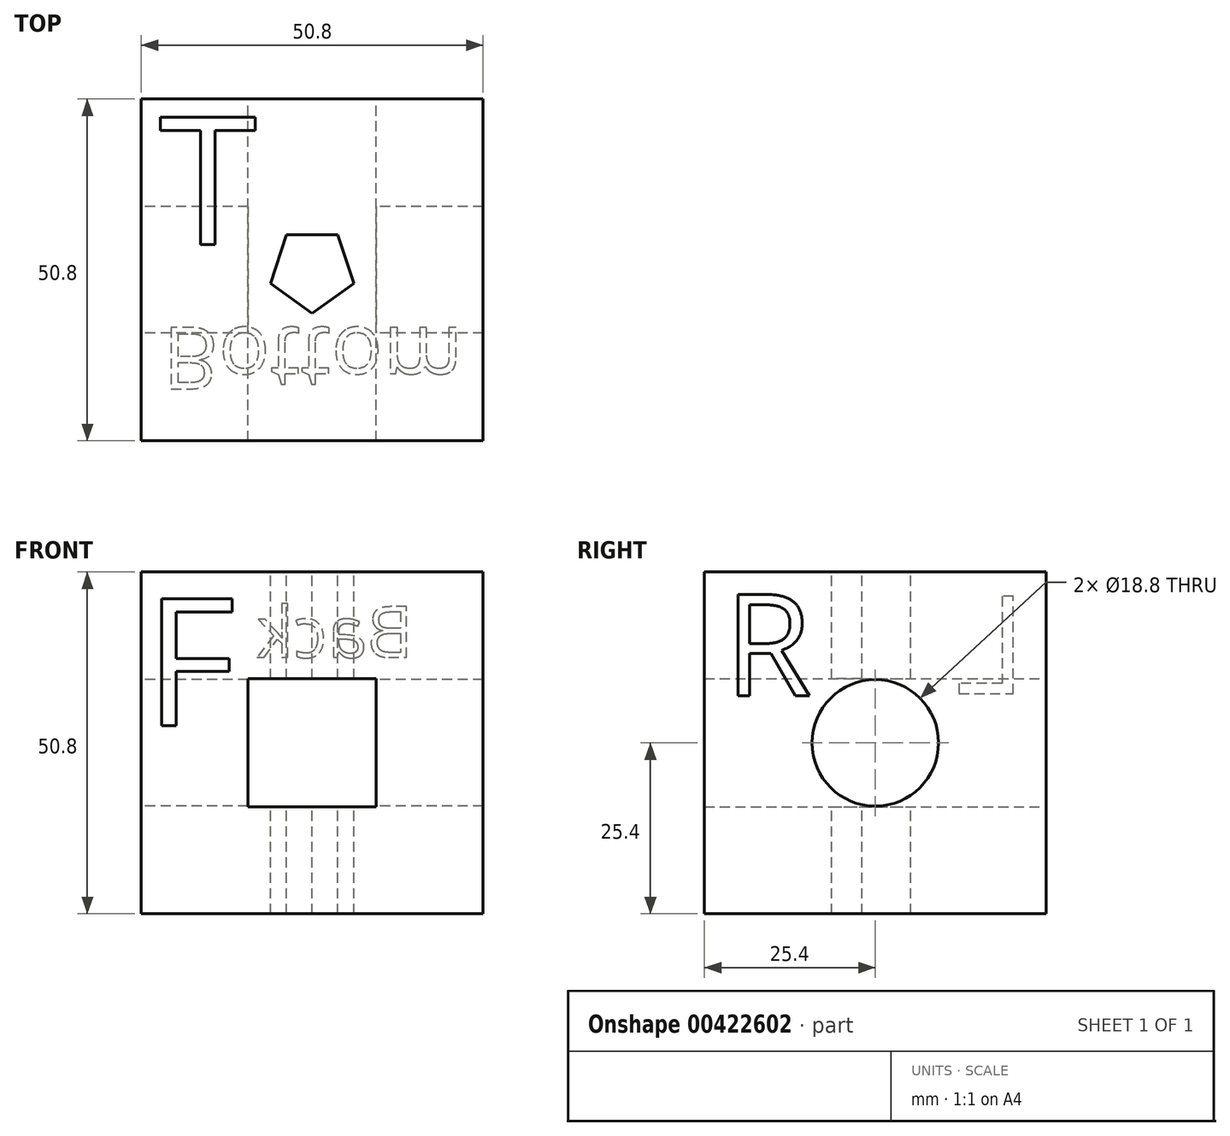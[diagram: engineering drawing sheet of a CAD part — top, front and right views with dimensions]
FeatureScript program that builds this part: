
annotation { "Feature Type Name" : "Feature", "Feature Type Description" : "" }
export const myFeature = defineFeature(function(context is Context, id is Id, definition is map)
    precondition{}
    {
        {
            var Q0;
            Q0=qCreatedBy(makeId("Front.planeOp"),FACE);
            var sketch = newSketch(context, id + "F0", { "sketchPlane" : qUnion([Q0])});
            skLineSegment(sketch, "E0.bottom", {"start": v(25.4, 25.4) * mm, "end": v(-25.4, 25.4) * mm});
            skLineSegment(sketch, "E0.top", {"start": v(25.4, -25.4) * mm, "end": v(-25.4, -25.4) * mm});
            skLineSegment(sketch, "E0.left", {"start": v(25.4, 25.4) * mm, "end": v(25.4, -25.4) * mm});
            skLineSegment(sketch, "E0.right", {"start": v(-25.4, 25.4) * mm, "end": v(-25.4, -25.4) * mm});
            skPoint(sketch, "E0.middle", {"position": v(0, 0) * mm});
            skLineSegment(sketch, "E1.bottom", {"start": v(9.52, 9.52) * mm, "end": v(-9.53, 9.52) * mm});
            skLineSegment(sketch, "E1.top", {"start": v(9.52, -9.52) * mm, "end": v(-9.53, -9.52) * mm});
            skLineSegment(sketch, "E1.left", {"start": v(9.52, 9.52) * mm, "end": v(9.52, -9.52) * mm});
            skLineSegment(sketch, "E1.right", {"start": v(-9.53, 9.52) * mm, "end": v(-9.53, -9.52) * mm});
            skSolve(sketch);
        }
        {
            var Q0;
            Q0=makeQuery(id+"F0.imprint","IMPRINT",FACE,{"disambiguationData":[TD([[makeQuery(id+"F0.imprint","IMPRINT",EDGE,{"derivedFrom":sQuery(id+"F0.wireOp",EDGE,"E0.bottom")}),1.0]])]});
            extrude(context, id + "F1", {"entities" : qUnion([Q0]), "depth" : 50.8 * mm, "symmetric" : true});
        }
        {
            var Q0;
            Q0=qCreatedBy(makeId("Right.planeOp"),FACE);
            var sketch = newSketch(context, id + "F2", { "sketchPlane" : qUnion([Q0])});
            skCircle(sketch, "E2", {"center": v(0, 0) * mm, "radius": 9.4 * mm});
            skSolve(sketch);
        }
        {
            var Q0;
            Q0=qSketchRegion(id+"F2",true);
            extrude(context, id + "F3", {"entities" : qUnion([Q0]), "operationType" : NewBodyOperationType.REMOVE, "depth" : 76.2 * mm, "symmetric" : true});
        }
        {
            var Q0;
            Q0=qCreatedBy(makeId("Top.planeOp"),FACE);
            var sketch = newSketch(context, id + "F4", { "sketchPlane" : qUnion([Q0])});
            skCircle(sketch, "E3.cCircle", {"center": v(0, 0) * mm, "radius": 5.24 * mm, "construction": true});
            skLineSegment(sketch, "E3.0", {"start": v(-3.8, 5.24) * mm, "end": v(3.8, 5.24) * mm});
            skLineSegment(sketch, "E3.1", {"start": v(3.8, 5.24) * mm, "end": v(6.16, -2) * mm});
            skLineSegment(sketch, "E3.2", {"start": v(6.16, -2) * mm, "end": v(0, -6.48) * mm});
            skLineSegment(sketch, "E3.3", {"start": v(0, -6.48) * mm, "end": v(-6.16, -2) * mm});
            skLineSegment(sketch, "E3.4", {"start": v(-6.16, -2) * mm, "end": v(-3.81, 5.24) * mm});
            skPoint(sketch, "E3.0.midPoint", {"position": v(0, 5.24) * mm});
            skSolve(sketch);
        }
        {
            var Q0;
            Q0=qSketchRegion(id+"F4",true);
            extrude(context, id + "F5", {"entities" : qUnion([Q0]), "operationType" : NewBodyOperationType.REMOVE, "oppositeDirection" : true, "depth" : 76.2 * mm, "symmetric" : true});
        }
        {
            var Q0;
            Q0=makeQuery(id+"F1.opExtrude","CAP_FACE",FACE,{"disambiguationData":[OSD([sQuery(id+"F0.wireOp",EDGE,"E0.bottom"),sQuery(id+"F0.wireOp",EDGE,"E0.top"),sQuery(id+"F0.wireOp",EDGE,"E0.left"),sQuery(id+"F0.wireOp",EDGE,"E0.right"),sQuery(id+"F0.wireOp",EDGE,"E1.bottom"),sQuery(id+"F0.wireOp",EDGE,"E1.top"),sQuery(id+"F0.wireOp",EDGE,"E1.left"),sQuery(id+"F0.wireOp",EDGE,"E1.right")])],"isStart":false});
            var sketch = newSketch(context, id + "F6", { "sketchPlane" : qUnion([Q0])});
            skText(sketch, "E4", { "text": "F", "fontName": "OpenSans-Regular.ttf"});
            const initialGuessF6  = {"E4": [-0.025, 0.00254, 1, 0, 0.01905]};
            skSetInitialGuess(sketch, initialGuessF6);
            skSolve(sketch);
        }
        {
            var Q0;
            Q0=qSketchRegion(id+"F6",true);
            extrude(context, id + "F7", {"entities" : qUnion([Q0]), "operationType" : NewBodyOperationType.REMOVE, "oppositeDirection" : true, "depth" : 0.03 * mm});
        }
        {
            var Q0;
            Q0=makeQuery(id+"F1.opExtrude","SWEPT_FACE",FACE,{"disambiguationData":[OSD([sQuery(id+"F0.wireOp",EDGE,"E0.bottom")])]});
            var sketch = newSketch(context, id + "F8", { "sketchPlane" : qUnion([Q0])});
            skText(sketch, "E5", { "text": "T", "fontName": "OpenSans-Regular.ttf"});
            const initialGuessF8  = {"E5": [-0.02283, 0.00378, 1, 0, 0.01905]};
            skSetInitialGuess(sketch, initialGuessF8);
            skSolve(sketch);
        }
        {
            var Q0;
            Q0=qSketchRegion(id+"F8",true);
            extrude(context, id + "F9", {"entities" : qUnion([Q0]), "operationType" : NewBodyOperationType.REMOVE, "oppositeDirection" : true, "depth" : 0.03 * mm});
        }
        {
            var Q0;
            Q0=makeQuery(id+"F1.opExtrude","CAP_FACE",FACE,{"disambiguationData":[OSD([sQuery(id+"F0.wireOp",EDGE,"E0.bottom"),sQuery(id+"F0.wireOp",EDGE,"E0.top"),sQuery(id+"F0.wireOp",EDGE,"E0.left"),sQuery(id+"F0.wireOp",EDGE,"E0.right"),sQuery(id+"F0.wireOp",EDGE,"E1.bottom"),sQuery(id+"F0.wireOp",EDGE,"E1.top"),sQuery(id+"F0.wireOp",EDGE,"E1.left"),sQuery(id+"F0.wireOp",EDGE,"E1.right")])],"isStart":true});
            var sketch = newSketch(context, id + "F10", { "sketchPlane" : qUnion([Q0])});
            skText(sketch, "E6", { "text": "Back", "fontName": "OpenSans-Regular.ttf"});
            const initialGuessF10  = {"E6": [-0.01502, 0.0127, 1, 0, 0.00762]};
            skSetInitialGuess(sketch, initialGuessF10);
            skSolve(sketch);
        }
        {
            var Q0;
            Q0=qSketchRegion(id+"F10",true);
            extrude(context, id + "F11", {"entities" : qUnion([Q0]), "operationType" : NewBodyOperationType.REMOVE, "oppositeDirection" : true, "depth" : 0.03 * mm});
        }
        {
            var Q0;
            Q0=makeQuery(id+"F1.opExtrude","SWEPT_FACE",FACE,{"disambiguationData":[OSD([sQuery(id+"F0.wireOp",EDGE,"E0.top")])]});
            var sketch = newSketch(context, id + "F12", { "sketchPlane" : qUnion([Q0])});
            skText(sketch, "E7", { "text": "Bottom", "fontName": "OpenSans-Regular.ttf"});
            const initialGuessF12  = {"E7": [-0.02223, 0.00857, 1, 0, 0.0092]};
            skSetInitialGuess(sketch, initialGuessF12);
            skSolve(sketch);
        }
        {
            var Q0;
            Q0=qSketchRegion(id+"F12",true);
            extrude(context, id + "F13", {"entities" : qUnion([Q0]), "operationType" : NewBodyOperationType.REMOVE, "oppositeDirection" : true, "depth" : 0.03 * mm});
        }
        {
            var Q0;
            Q0=makeQuery(id+"F1.opExtrude","SWEPT_FACE",FACE,{"disambiguationData":[OSD([sQuery(id+"F0.wireOp",EDGE,"E0.right")])]});
            var sketch = newSketch(context, id + "F14", { "sketchPlane" : qUnion([Q0])});
            skText(sketch, "E8", { "text": "L", "fontName": "OpenSans-Regular.ttf"});
            const initialGuessF14  = {"E8": [-0.0225, 0.0073, 1, 0, 0.0146]};
            skSetInitialGuess(sketch, initialGuessF14);
            skSolve(sketch);
        }
        {
            var Q0;
            Q0=qSketchRegion(id+"F14",true);
            extrude(context, id + "F15", {"entities" : qUnion([Q0]), "operationType" : NewBodyOperationType.REMOVE, "oppositeDirection" : true, "depth" : 0.03 * mm});
        }
        {
            var Q0;
            Q0=makeQuery(id+"F1.opExtrude","SWEPT_FACE",FACE,{"disambiguationData":[OSD([sQuery(id+"F0.wireOp",EDGE,"E0.left")])]});
            var sketch = newSketch(context, id + "F16", { "sketchPlane" : qUnion([Q0])});
            skText(sketch, "E9", { "text": "R", "fontName": "OpenSans-Regular.ttf"});
            const initialGuessF16  = {"E9": [-0.0225, 0.007, 1, 0, 0.0152]};
            skSetInitialGuess(sketch, initialGuessF16);
            skSolve(sketch);
        }
        {
            var Q0;
            Q0=qSketchRegion(id+"F16",true);
            extrude(context, id + "F17", {"entities" : qUnion([Q0]), "operationType" : NewBodyOperationType.REMOVE, "oppositeDirection" : true, "depth" : 0.03 * mm});
        }
    });
